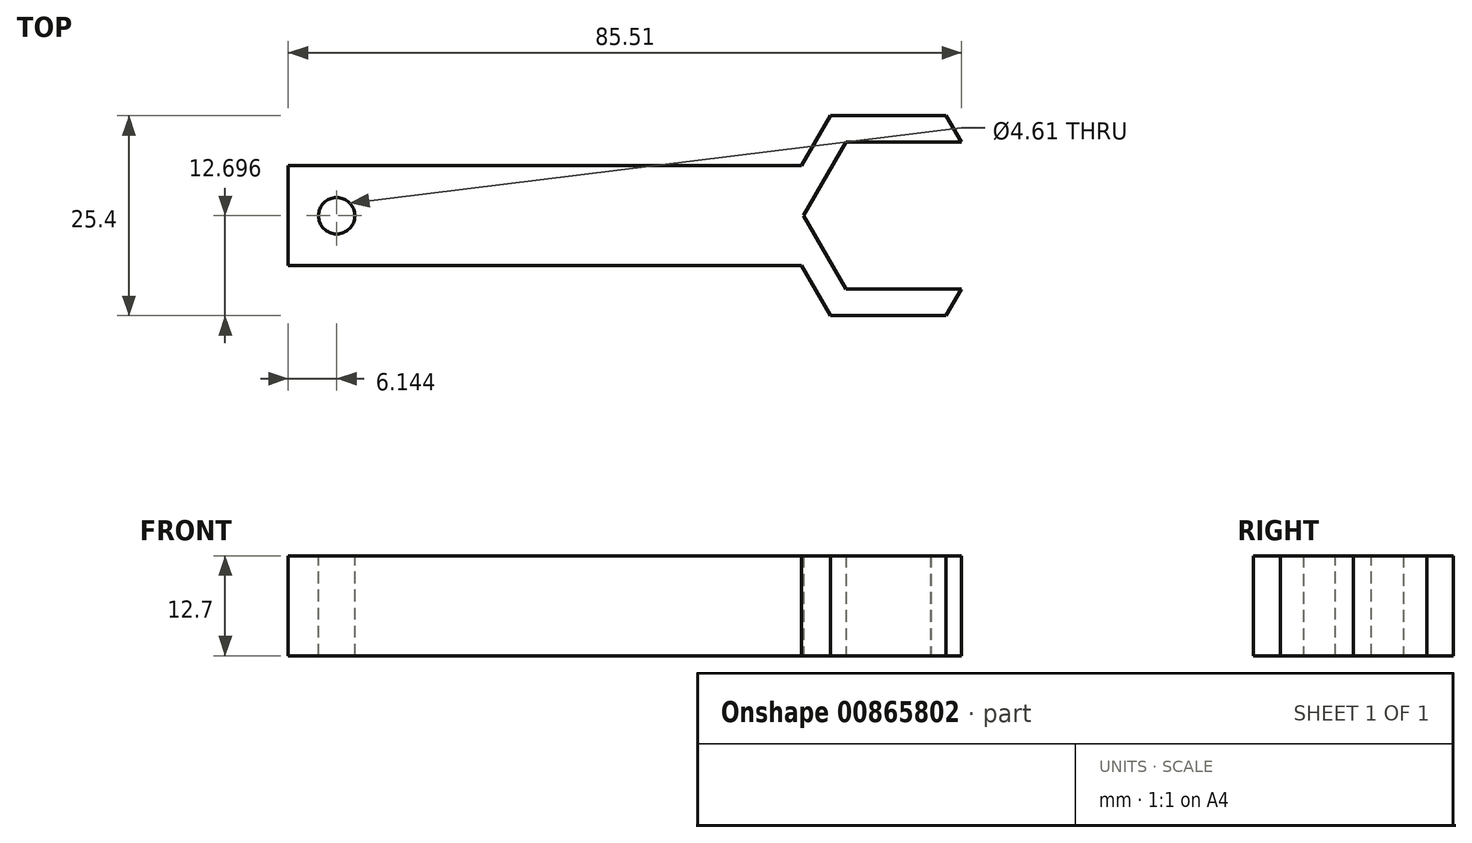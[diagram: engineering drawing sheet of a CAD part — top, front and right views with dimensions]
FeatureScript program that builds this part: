
annotation { "Feature Type Name" : "Feature", "Feature Type Description" : "" }
export const myFeature = defineFeature(function(context is Context, id is Id, definition is map)
    precondition{}
    {
        {
            var Q0;
            Q0=qCreatedBy(makeId("Top.planeOp"),FACE);
            var sketch = newSketch(context, id + "F0", { "sketchPlane" : qUnion([Q0])});
            skLineSegment(sketch, "E0.bottom", {"start": v(-38.68, -17.54) * mm, "end": v(26.53, -17.54) * mm});
            skLineSegment(sketch, "E0.top", {"start": v(-38.68, -30.24) * mm, "end": v(26.53, -30.24) * mm});
            skLineSegment(sketch, "E0.left", {"start": v(-38.68, -17.54) * mm, "end": v(-38.68, -30.24) * mm});
            skCircle(sketch, "E1.cCircle", {"center": v(37.52, -23.9) * mm, "radius": 12.7 * mm, "construction": true});
            skLineSegment(sketch, "E1.0", {"start": v(44.86, -36.6) * mm, "end": v(30.2, -36.6) * mm});
            skLineSegment(sketch, "E1.1", {"start": v(30.2, -36.6) * mm, "end": v(26.53, -30.24) * mm});
            skLineSegment(sketch, "E1.2", {"start": v(26.53, -17.54) * mm, "end": v(30.2, -11.2) * mm});
            skLineSegment(sketch, "E1.3", {"start": v(30.2, -11.2) * mm, "end": v(44.86, -11.2) * mm});
            skLineSegment(sketch, "E1.4", {"start": v(44.86, -11.2) * mm, "end": v(46.8, -14.56) * mm});
            skLineSegment(sketch, "E1.5", {"start": v(46.83, -33.18) * mm, "end": v(44.86, -36.6) * mm});
            skPoint(sketch, "E1.0.midPoint", {"position": v(37.52, -36.6) * mm});
            skPoint(sketch, "E2.orphan", {"position": v(37.52, -30.24) * mm});
            skPoint(sketch, "E3.orphan", {"position": v(37.52, -17.54) * mm});
            skPoint(sketch, "E4.orphan", {"position": v(22.86, -23.9) * mm});
            skCircle(sketch, "E5.cCircle", {"center": v(37.52, -23.9) * mm, "radius": 9.33 * mm, "construction": true});
            skLineSegment(sketch, "E5.1", {"start": v(42.91, -33.23) * mm, "end": v(32.14, -33.23) * mm});
            skLineSegment(sketch, "E5.2", {"start": v(32.14, -33.23) * mm, "end": v(26.75, -23.9) * mm});
            skLineSegment(sketch, "E5.3", {"start": v(26.75, -23.9) * mm, "end": v(32.14, -14.56) * mm});
            skLineSegment(sketch, "E5.4", {"start": v(32.14, -14.56) * mm, "end": v(42.91, -14.56) * mm});
            skPoint(sketch, "E5.0.midPoint", {"position": v(45.6, -28.56) * mm});
            skLineSegment(sketch, "E6.bottom", {"start": v(32.14, -14.56) * mm, "end": v(46.8, -14.56) * mm});
            skLineSegment(sketch, "E6.top", {"start": v(32.14, -33.18) * mm, "end": v(46.83, -33.18) * mm});
            skPoint(sketch, "E7.orphan", {"position": v(52.19, -23.9) * mm});
            skLineSegment(sketch, "E8.trimOffspring", {"start": v(42.94, -33.18) * mm, "end": v(42.91, -33.23) * mm});
            skPoint(sketch, "E9.orphan", {"position": v(48.3, -23.9) * mm});
            skSolve(sketch);
        }
        {
            var Q0;
            Q0 = qSketchRegion(id + "F0", true);
            extrude(context, id + "F1", {"entities" : qUnion([Q0]), "depth" : 12.7 * mm, "offsetDistance" : 25.4 * mm});
        }
        {
            var Q0;
            Q0=makeQuery(id+"F1.opExtrude","CAP_FACE",FACE,{"disambiguationData":[OSD([sQuery(id+"F0.wireOp",EDGE,"E0.bottom"),sQuery(id+"F0.wireOp",EDGE,"E0.top"),sQuery(id+"F0.wireOp",EDGE,"E0.left"),sQuery(id+"F0.wireOp",EDGE,"E1.0"),sQuery(id+"F0.wireOp",EDGE,"E1.1"),sQuery(id+"F0.wireOp",EDGE,"E1.2"),sQuery(id+"F0.wireOp",EDGE,"E1.3"),sQuery(id+"F0.wireOp",EDGE,"E1.4"),sQuery(id+"F0.wireOp",EDGE,"E1.5"),sQuery(id+"F0.wireOp",EDGE,"E5.1"),sQuery(id+"F0.wireOp",EDGE,"E5.2"),sQuery(id+"F0.wireOp",EDGE,"E5.3"),sQuery(id+"F0.wireOp",EDGE,"E6.bottom"),sQuery(id+"F0.wireOp",EDGE,"E6.top"),sQuery(id+"F0.wireOp",EDGE,"E8.trimOffspring")])],"isStart":false});
            var sketch = newSketch(context, id + "F2", { "sketchPlane" : qUnion([Q0])});
            skCircle(sketch, "E10", {"center": v(-32.54, -23.9) * mm, "radius": 2.3 * mm});
            skPoint(sketch, "E10.centerSnap0", {"position": v(-38.68, -23.9) * mm});
            skSolve(sketch);
        }
        {
            var Q0;
            Q0=makeQuery(id+"F2.imprint","IMPRINT",FACE,{"disambiguationData":[TD([[makeQuery(id+"F2.imprint","IMPRINT",EDGE,{"derivedFrom":sQuery(id+"F2.wireOp",EDGE,"E10")}),1.0]])]});
            extrude(context, id + "F3", {"entities" : qUnion([Q0]), "operationType" : NewBodyOperationType.REMOVE, "oppositeDirection" : true, "depth" : 25.4 * mm, "offsetDistance" : 25.4 * mm});
        }
    });
